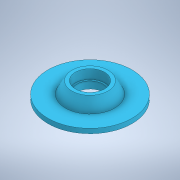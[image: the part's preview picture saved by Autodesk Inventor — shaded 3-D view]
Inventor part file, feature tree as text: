
AUTODESK INVENTOR PART (.ipt)
format: ipt  version: 2022.2 (Build 262287000, 287)  size: 124,416 bytes
history: native  units: mm
features: revolve x1, sketch x1
ambient origin geometry x8: Origin, YZ Plane, XZ Plane, XY Plane, X Axis, Y Axis, Z Axis, Center Point
bodies: Solid1 (feature_tree)
feature tree (2):
  revolve  "Revolution1"  [1 undecoded]
  sketch  "Sketch2"  dims[d0=12.5mm d1=1.5mm d2=3.0mm d3=25.0mm d4=6.0mm d5=8.0mm d6=0.0mm d7=4.0mm d8=15.0mm d9=90.0deg]
note: 1 required parameter value undecoded (feature->parameter linkage not recoverable at this tier; creation-order binding heuristic only, values carry confidence <= 0.55)
